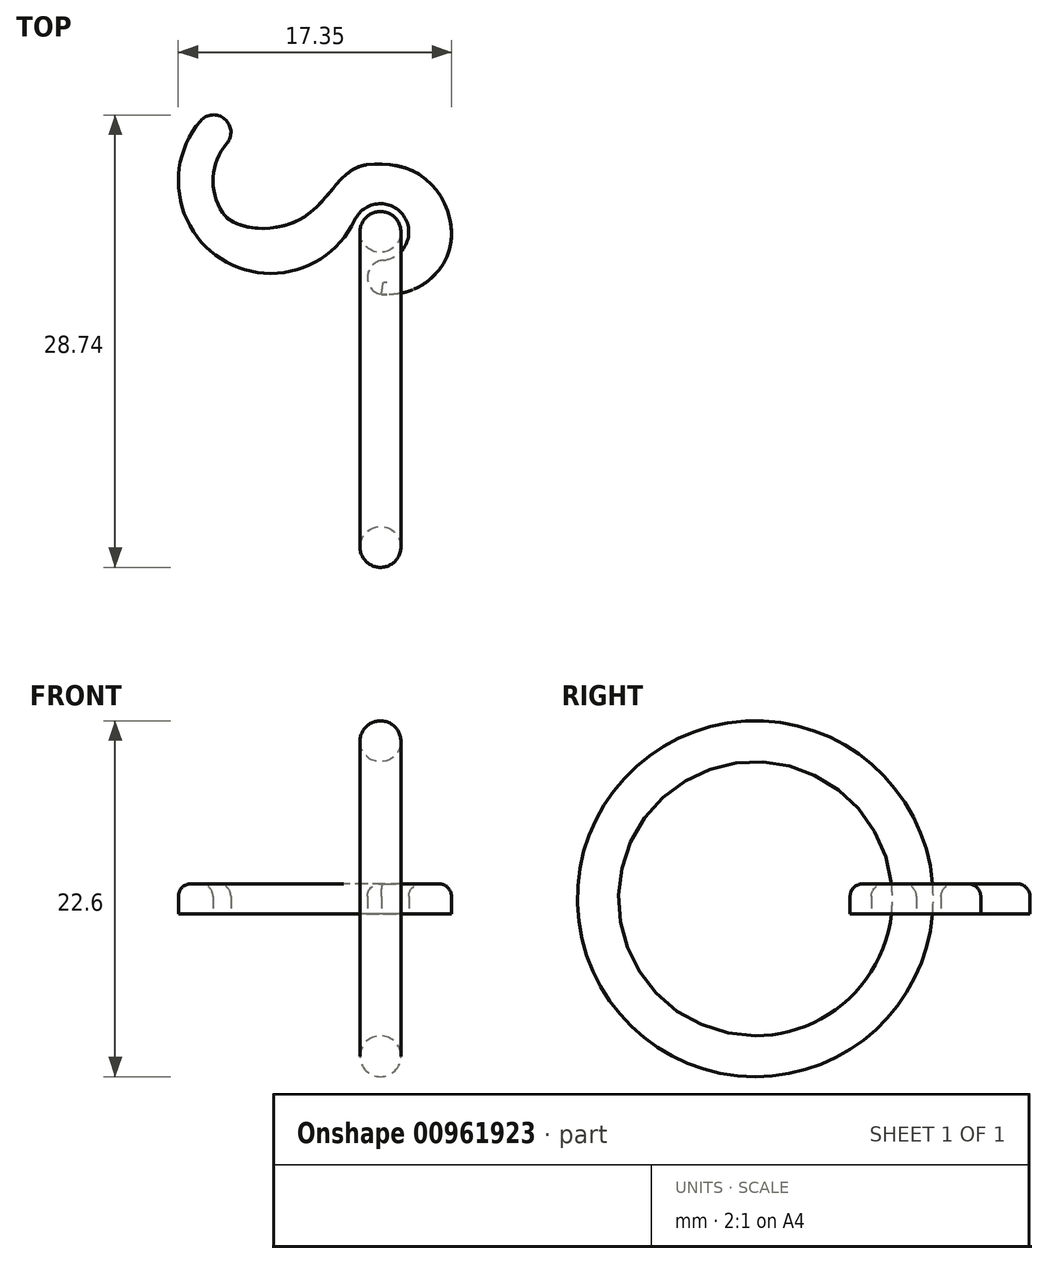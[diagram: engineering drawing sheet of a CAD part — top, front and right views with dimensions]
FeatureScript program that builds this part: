
annotation { "Feature Type Name" : "Feature", "Feature Type Description" : "" }
export const myFeature = defineFeature(function(context is Context, id is Id, definition is map)
    precondition{}
    {
        {
            var Q0;
            Q0=qCreatedBy(makeId("Top.planeOp"),FACE);
            var sketch = newSketch(context, id + "F0", { "sketchPlane" : qUnion([Q0])});
            skCircle(sketch, "E0", {"center": v(0, 10) * mm, "radius": 1.3 * mm});
            skLineSegment(sketch, "E1", {"start": v(0, 0) * mm, "end": v(-2.82, 0) * mm, "construction": true});
            skArc(sketch, "E2", {"start": v(0.27, 7.11) * mm, "mid": v(2.37, 11.67) * mm, "end": v(-2.63, 11.23) * mm});
            skArc(sketch, "E3.filletArc", {"start": v(-10.6, 16.34) * mm, "mid": v(-9.54, 9.23) * mm, "end": v(-2.63, 11.23) * mm});
            skLineSegment(sketch, "E4", {"start": v(0, 10) * mm, "end": v(-1.64, 5.37) * mm, "construction": true});
            skLineSegment(sketch, "E5", {"start": v(-0.83, 7.67) * mm, "end": v(-1.52, 5.72) * mm});
            skPoint(sketch, "E6.visualSharp", {"position": v(-0.97, 7.27) * mm});
            skArc(sketch, "E6.filletArc", {"start": v(0.27, 7.11) * mm, "mid": v(-0.83, 6.68) * mm, "end": v(-1.52, 5.72) * mm});
            skArc(sketch, "E7", {"start": v(-10.6, 16.34) * mm, "mid": v(-9.29, 17.42) * mm, "end": v(-7.69, 17.97) * mm});
            skArc(sketch, "E8", {"start": v(-7.69, 17.97) * mm, "mid": v(-5.06, 16.97) * mm, "end": v(-4.56, 14.21) * mm});
            skArc(sketch, "E9.0.startCap", {"start": v(-7.52, 16.88) * mm, "mid": v(-8.77, 17.8) * mm, "end": v(-7.85, 19.06) * mm});
            skArc(sketch, "E9.0.endCap", {"start": v(-3.52, 13.85) * mm, "mid": v(-4.92, 13.17) * mm, "end": v(-5.6, 14.57) * mm});
            skArc(sketch, "E9.0.left", {"start": v(-7.85, 19.06) * mm, "mid": v(-4.21, 17.68) * mm, "end": v(-3.52, 13.85) * mm});
            skArc(sketch, "E9.0.right", {"start": v(-7.52, 16.88) * mm, "mid": v(-5.9, 16.27) * mm, "end": v(-5.6, 14.57) * mm});
            skArc(sketch, "E9.1.startCap", {"start": v(-9.76, 15.63) * mm, "mid": v(-11.31, 15.5) * mm, "end": v(-11.44, 17.05) * mm});
            skArc(sketch, "E9.1.endCap", {"start": v(-7.85, 19.06) * mm, "mid": v(-6.6, 18.14) * mm, "end": v(-7.52, 16.88) * mm});
            skArc(sketch, "E9.1.left", {"start": v(-11.44, 17.05) * mm, "mid": v(-9.83, 18.38) * mm, "end": v(-7.85, 19.06) * mm});
            skArc(sketch, "E9.1.right", {"start": v(-9.76, 15.63) * mm, "mid": v(-8.75, 16.46) * mm, "end": v(-7.52, 16.88) * mm});
            skArc(sketch, "E9.2.startCap", {"start": v(-11.44, 17.05) * mm, "mid": v(-9.89, 17.18) * mm, "end": v(-9.76, 15.63) * mm});
            skArc(sketch, "E9.2.left", {"start": v(-9.76, 15.63) * mm, "mid": v(-10.63, 13.48) * mm, "end": v(-10.04, 11.24) * mm});
            skArc(sketch, "E9.2.right", {"start": v(-11.44, 17.05) * mm, "mid": v(-10.13, 8.3) * mm, "end": v(-1.63, 10.76) * mm});
            skArc(sketch, "E9.3.startCap", {"start": v(0.07, 6.03) * mm, "mid": v(-0.83, 7.16) * mm, "end": v(0.17, 8.2) * mm});
            skArc(sketch, "E9.3.left", {"start": v(0.17, 8.2) * mm, "mid": v(1.47, 11.04) * mm, "end": v(-1.63, 10.76) * mm});
            skFitSpline(sketch, "E10", {"points": [v(-10.04, 11.24) * mm, v(-5.03, 10.85) * mm, v(-0.87, 14.27) * mm], "startDerivative": vector(4.6, -7.08) * mm, "endDerivative": vector(9.85, 1.05) * mm});
            skArc(sketch, "E11.0.startCap", {"start": v(0.17, 8.2) * mm, "mid": v(1.36, 7.21) * mm, "end": v(0.37, 6.02) * mm});
            skArc(sketch, "E11.0.endCap", {"start": v(-0.48, 5.35) * mm, "mid": v(-1.89, 4.69) * mm, "end": v(-2.55, 6.09) * mm});
            skArc(sketch, "E11.0.left", {"start": v(0.37, 6.02) * mm, "mid": v(-0.15, 5.81) * mm, "end": v(-0.48, 5.35) * mm});
            skArc(sketch, "E11.0.right", {"start": v(0.17, 8.2) * mm, "mid": v(-1.5, 7.55) * mm, "end": v(-2.55, 6.09) * mm});
            skFitSpline(sketch, "E12", {"points": [v(-0.87, 14.27) * mm, v(2.63, 13.55) * mm, v(4.47, 9.32) * mm, v(0.07, 6.03) * mm], "startDerivative": vector(11.12, 1.18) * mm, "endDerivative": vector(-20.1, 1.27) * mm});
            skCircle(sketch, "E13", {"center": v(-3.16, 13.5) * mm, "radius": 0.5 * mm, "construction": true});
            skSolve(sketch);
        }
        {
            var Q0;
            Q0=makeQuery(id+"F0.imprint","IMPRINT",FACE,{"disambiguationData":[TD([[makeQuery(id+"F0.imprint","IMPRINT",EDGE,{"derivedFrom":sQuery(id+"F0.wireOp",EDGE,"E0")}),1.0]])]});
            var Q1;
            Q1=sQuery(id+"F0.wireOp",EDGE,"E1");
            revolve(context, id + "F1", {"surfaceOperationType" : NewSurfaceOperationType.NEW, "entities" : qUnion([Q0]), "axis" : qUnion([Q1]), "revolveType" : RevolveType.FULL});
        }
        {
            var Q0;
            {var subQ0=sQuery(id+"F0.wireOp",EDGE,"7e8b46de-5f97-4e43-a4e6-41a7d2c543f1.filletArc");var subQ1=sQuery(id+"F0.wireOp",EDGE,"XuSTN1GD-owKZ-Hfnf-Vevz-HP5xYmG9djur");var subQ2=makeQuery(id+"F0.imprint","INTERSECT",VERTEX,{"derivedFrom":[subQ1,subQ0]});Q0=makeQuery(id+"F0.imprint","IMPRINT",FACE,{"disambiguationData":[TD([[makeQuery(id+"F0.imprint","IMPRINT",EDGE,{"disambiguationData":[TD([[subQ2,-1.0]])],"derivedFrom":subQ1}),1.0]])]});}
            var Q1;
            {var subQ0=sQuery(id+"F0.wireOp",EDGE,"E6.filletArc");var subQ1=sQuery(id+"F0.wireOp",EDGE,"E2");var subQ2=makeQuery(id+"F0.imprint","INTERSECT",VERTEX,{"derivedFrom":[subQ1,subQ0]});Q1=makeQuery(id+"F0.imprint","IMPRINT",FACE,{"disambiguationData":[TD([[makeQuery(id+"F0.imprint","IMPRINT",EDGE,{"disambiguationData":[TD([[subQ2,-1.0]])],"derivedFrom":subQ1}),-1.0]])]});}
            var Q2;
            Q2=makeQuery(id+"F0.imprint","IMPRINT",FACE,{"disambiguationData":[TD([[makeQuery(id+"F0.imprint","IMPRINT",EDGE,{"derivedFrom":sQuery(id+"F0.wireOp",EDGE,"7d60ddda-c9f3-4b5c-aec7-61beb639432c.6.endCap")}),-1.0]])]});
            var Q3;
            {var subQ0=sQuery(id+"F0.wireOp",EDGE,"E3.filletArc");var subQ1=sQuery(id+"F0.wireOp",EDGE,"E2");var subQ2=makeQuery(id+"F0.imprint","INTERSECT",VERTEX,{"derivedFrom":[subQ1,subQ0]});Q3=makeQuery(id+"F0.imprint","IMPRINT",FACE,{"disambiguationData":[TD([[makeQuery(id+"F0.imprint","IMPRINT",EDGE,{"disambiguationData":[TD([[subQ2,1.0]])],"derivedFrom":subQ1}),-1.0]])]});}
            var Q4;
            {var subQ0=sQuery(id+"F0.wireOp",EDGE,"E6.filletArc");var subQ1=sQuery(id+"F0.wireOp",EDGE,"E2");var subQ2=makeQuery(id+"F0.imprint","INTERSECT",VERTEX,{"derivedFrom":[subQ1,subQ0]});Q4=makeQuery(id+"F0.imprint","IMPRINT",FACE,{"disambiguationData":[TD([[makeQuery(id+"F0.imprint","IMPRINT",EDGE,{"disambiguationData":[TD([[subQ2,-1.0]])],"derivedFrom":subQ1}),1.0]])]});}
            var Q5;
            {var subQ0=sQuery(id+"F0.wireOp",EDGE,"2rV7FZ9r-o5Y1-5ZDM-YBhN-Ku4Qg7FZG19c");var subQ1=sQuery(id+"F0.wireOp",EDGE,"XuSTN1GD-owKZ-Hfnf-Vevz-HP5xYmG9djur");var subQ2=makeQuery(id+"F0.imprint","INTERSECT",VERTEX,{"derivedFrom":[subQ1,subQ0]});Q5=makeQuery(id+"F0.imprint","IMPRINT",FACE,{"disambiguationData":[TD([[makeQuery(id+"F0.imprint","IMPRINT",EDGE,{"disambiguationData":[TD([[subQ2,1.0]])],"derivedFrom":subQ1}),1.0]])]});}
            var Q6;
            {var subQ5=sQuery(id+"F0.wireOp",EDGE,"7d60ddda-c9f3-4b5c-aec7-61beb639432c.2.right");Q6=makeQuery(id+"F0.imprint","IMPRINT",FACE,{"disambiguationData":[TD([[makeQuery(id+"F0.imprint","IMPRINT",EDGE,{"derivedFrom":subQ5}),1.0]])]});}
            var Q7;
            {var subQ5=sQuery(id+"F0.wireOp",EDGE,"gjqhSW9i-IF4X-P20h-zRvC-4p3DaIg5BdPQ");Q7=makeQuery(id+"F0.imprint","IMPRINT",FACE,{"disambiguationData":[TD([[makeQuery(id+"F0.imprint","IMPRINT",EDGE,{"derivedFrom":subQ5}),-1.0]])]});}
            var Q8;
            {var subQ0=sQuery(id+"F0.wireOp",EDGE,"7d60ddda-c9f3-4b5c-aec7-61beb639432c.2.endCap");var subQ1=sQuery(id+"F0.wireOp",EDGE,"E3.filletArc");var subQ2=makeQuery(id+"F0.imprint","INTERSECT",VERTEX,{"derivedFrom":[subQ1,subQ0]});Q8=makeQuery(id+"F0.imprint","IMPRINT",FACE,{"disambiguationData":[TD([[makeQuery(id+"F0.imprint","IMPRINT",EDGE,{"disambiguationData":[TD([[subQ2,-1.0]])],"derivedFrom":subQ1}),-1.0]])]});}
            var Q9;
            {var subQ0=sQuery(id+"F0.wireOp",EDGE,"E3.filletArc");var subQ1=sQuery(id+"F0.wireOp",EDGE,"E2");var subQ2=makeQuery(id+"F0.imprint","INTERSECT",VERTEX,{"derivedFrom":[subQ1,subQ0]});Q9=makeQuery(id+"F0.imprint","IMPRINT",FACE,{"disambiguationData":[TD([[makeQuery(id+"F0.imprint","IMPRINT",EDGE,{"disambiguationData":[TD([[subQ2,1.0]])],"derivedFrom":subQ1}),1.0]])]});}
            var Q10;
            {var subQ5=sQuery(id+"F0.wireOp",EDGE,"7d60ddda-c9f3-4b5c-aec7-61beb639432c.4.left");Q10=makeQuery(id+"F0.imprint","IMPRINT",FACE,{"disambiguationData":[TD([[makeQuery(id+"F0.imprint","IMPRINT",EDGE,{"derivedFrom":subQ5}),-1.0]])]});}
            var Q11;
            {var subQ7=sQuery(id+"F0.wireOp",EDGE,"gjqhSW9i-IF4X-P20h-zRvC-4p3DaIg5BdPQ");Q11=makeQuery(id+"F0.imprint","IMPRINT",FACE,{"disambiguationData":[TD([[makeQuery(id+"F0.imprint","IMPRINT",EDGE,{"derivedFrom":subQ7}),1.0]])]});}
            var Q12;
            {var subQ0=sQuery(id+"F0.wireOp",EDGE,"2rV7FZ9r-o5Y1-5ZDM-YBhN-Ku4Qg7FZG19c");var subQ1=sQuery(id+"F0.wireOp",EDGE,"XuSTN1GD-owKZ-Hfnf-Vevz-HP5xYmG9djur");var subQ2=makeQuery(id+"F0.imprint","INTERSECT",VERTEX,{"derivedFrom":[subQ1,subQ0]});Q12=makeQuery(id+"F0.imprint","IMPRINT",FACE,{"disambiguationData":[TD([[makeQuery(id+"F0.imprint","IMPRINT",EDGE,{"disambiguationData":[TD([[subQ2,1.0]])],"derivedFrom":subQ1}),-1.0]])]});}
            var Q13;
            {var subQ5=sQuery(id+"F0.wireOp",EDGE,"7d60ddda-c9f3-4b5c-aec7-61beb639432c.1.right");Q13=makeQuery(id+"F0.imprint","IMPRINT",FACE,{"disambiguationData":[TD([[makeQuery(id+"F0.imprint","IMPRINT",EDGE,{"derivedFrom":subQ5}),1.0]])]});}
            var Q14;
            Q14=makeQuery(id+"F0.imprint","IMPRINT",FACE,{"disambiguationData":[TD([[makeQuery(id+"F0.imprint","IMPRINT",EDGE,{"derivedFrom":sQuery(id+"F0.wireOp",EDGE,"7d60ddda-c9f3-4b5c-aec7-61beb639432c.0.endCap")}),-1.0]])]});
            var Q15;
            {var subQ5=sQuery(id+"F0.wireOp",EDGE,"7d60ddda-c9f3-4b5c-aec7-61beb639432c.1.left");Q15=makeQuery(id+"F0.imprint","IMPRINT",FACE,{"disambiguationData":[TD([[makeQuery(id+"F0.imprint","IMPRINT",EDGE,{"derivedFrom":subQ5}),-1.0]])]});}
            var Q16;
            {var subQ5=sQuery(id+"F0.wireOp",EDGE,"7d60ddda-c9f3-4b5c-aec7-61beb639432c.5.left");Q16=makeQuery(id+"F0.imprint","IMPRINT",FACE,{"disambiguationData":[TD([[makeQuery(id+"F0.imprint","IMPRINT",EDGE,{"derivedFrom":subQ5}),-1.0]])]});}
            var Q17;
            {var subQ5=sQuery(id+"F0.wireOp",EDGE,"7d60ddda-c9f3-4b5c-aec7-61beb639432c.4.right");Q17=makeQuery(id+"F0.imprint","IMPRINT",FACE,{"disambiguationData":[TD([[makeQuery(id+"F0.imprint","IMPRINT",EDGE,{"derivedFrom":subQ5}),1.0]])]});}
            var Q18;
            {var subQ0=sQuery(id+"F0.wireOp",EDGE,"7e8b46de-5f97-4e43-a4e6-41a7d2c543f1.filletArc");var subQ1=sQuery(id+"F0.wireOp",EDGE,"XuSTN1GD-owKZ-Hfnf-Vevz-HP5xYmG9djur");var subQ2=makeQuery(id+"F0.imprint","INTERSECT",VERTEX,{"derivedFrom":[subQ1,subQ0]});Q18=makeQuery(id+"F0.imprint","IMPRINT",FACE,{"disambiguationData":[TD([[makeQuery(id+"F0.imprint","IMPRINT",EDGE,{"disambiguationData":[TD([[subQ2,-1.0]])],"derivedFrom":subQ1}),-1.0]])]});}
            var Q19;
            {var subQ5=sQuery(id+"F0.wireOp",EDGE,"7d60ddda-c9f3-4b5c-aec7-61beb639432c.5.right");Q19=makeQuery(id+"F0.imprint","IMPRINT",FACE,{"disambiguationData":[TD([[makeQuery(id+"F0.imprint","IMPRINT",EDGE,{"derivedFrom":subQ5}),1.0]])]});}
            var Q20;
            {var subQ5=sQuery(id+"F0.wireOp",EDGE,"7d60ddda-c9f3-4b5c-aec7-61beb639432c.2.left");Q20=makeQuery(id+"F0.imprint","IMPRINT",FACE,{"disambiguationData":[TD([[makeQuery(id+"F0.imprint","IMPRINT",EDGE,{"derivedFrom":subQ5}),-1.0]])]});}
            var Q21;
            {var subQ0=sQuery(id+"F0.wireOp",EDGE,"7d60ddda-c9f3-4b5c-aec7-61beb639432c.3.endCap");var subQ1=sQuery(id+"F0.wireOp",EDGE,"7e8b46de-5f97-4e43-a4e6-41a7d2c543f1.filletArc");var subQ2=makeQuery(id+"F0.imprint","INTERSECT",VERTEX,{"derivedFrom":[subQ1,subQ0]});Q21=makeQuery(id+"F0.imprint","IMPRINT",FACE,{"disambiguationData":[TD([[makeQuery(id+"F0.imprint","IMPRINT",EDGE,{"disambiguationData":[TD([[subQ2,-1.0]])],"derivedFrom":subQ1}),1.0]])]});}
            var Q22;
            {var subQ0=sQuery(id+"F0.wireOp",EDGE,"7d60ddda-c9f3-4b5c-aec7-61beb639432c.3.endCap");var subQ1=sQuery(id+"F0.wireOp",EDGE,"7e8b46de-5f97-4e43-a4e6-41a7d2c543f1.filletArc");var subQ2=makeQuery(id+"F0.imprint","INTERSECT",VERTEX,{"derivedFrom":[subQ1,subQ0]});Q22=makeQuery(id+"F0.imprint","IMPRINT",FACE,{"disambiguationData":[TD([[makeQuery(id+"F0.imprint","IMPRINT",EDGE,{"disambiguationData":[TD([[subQ2,-1.0]])],"derivedFrom":subQ1}),-1.0]])]});}
            var Q23;
            {var subQ0=sQuery(id+"F0.wireOp",EDGE,"7d60ddda-c9f3-4b5c-aec7-61beb639432c.2.endCap");var subQ1=sQuery(id+"F0.wireOp",EDGE,"E3.filletArc");var subQ2=makeQuery(id+"F0.imprint","INTERSECT",VERTEX,{"derivedFrom":[subQ1,subQ0]});Q23=makeQuery(id+"F0.imprint","IMPRINT",FACE,{"disambiguationData":[TD([[makeQuery(id+"F0.imprint","IMPRINT",EDGE,{"disambiguationData":[TD([[subQ2,-1.0]])],"derivedFrom":subQ1}),1.0]])]});}
            var Q24;
            {var subQ0=sQuery(id+"F0.wireOp",EDGE,"7d60ddda-c9f3-4b5c-aec7-61beb639432c.3.left");Q24=makeQuery(id+"F0.imprint","IMPRINT",FACE,{"disambiguationData":[TD([[makeQuery(id+"F0.imprint","IMPRINT",EDGE,{"derivedFrom":subQ0}),-1.0]])]});}
            var Q25;
            {var subQ0=sQuery(id+"F0.wireOp",EDGE,"7d60ddda-c9f3-4b5c-aec7-61beb639432c.3.right");Q25=makeQuery(id+"F0.imprint","IMPRINT",FACE,{"disambiguationData":[TD([[makeQuery(id+"F0.imprint","IMPRINT",EDGE,{"derivedFrom":subQ0}),1.0]])]});}
            var Q26;
            {var subQ0=sQuery(id+"F0.wireOp",EDGE,"3c797257-ffbf-45d1-a8b6-85a41e315347.0.startCap");var subQ1=sQuery(id+"F0.wireOp",EDGE,"E3.filletArc");var subQ2=makeQuery(id+"F0.imprint","INTERSECT",VERTEX,{"derivedFrom":[subQ1,subQ0]});Q26=makeQuery(id+"F0.imprint","IMPRINT",FACE,{"disambiguationData":[TD([[makeQuery(id+"F0.imprint","IMPRINT",EDGE,{"disambiguationData":[TD([[subQ2,-1.0]])],"derivedFrom":subQ1}),-1.0]])]});}
            var Q27;
            {var subQ0=sQuery(id+"F0.wireOp",EDGE,"0f0b0a7c-fbad-4233-8603-baac45b0bff0");var subQ1=sQuery(id+"F0.wireOp",EDGE,"E3.filletArc");var subQ2=makeQuery(id+"F0.imprint","INTERSECT",VERTEX,{"derivedFrom":[subQ1,subQ0]});Q27=makeQuery(id+"F0.imprint","IMPRINT",FACE,{"disambiguationData":[TD([[makeQuery(id+"F0.imprint","IMPRINT",EDGE,{"disambiguationData":[TD([[subQ2,-1.0]])],"derivedFrom":subQ1}),1.0]])]});}
            var Q28;
            {var subQ1=sQuery(id+"F0.wireOp",EDGE,"7d60ddda-c9f3-4b5c-aec7-61beb639432c.4.left");var subQ3=sQuery(id+"F0.wireOp",EDGE,"3c797257-ffbf-45d1-a8b6-85a41e315347.0.right");var subQ4=makeQuery(id+"F0.imprint","INTERSECT",VERTEX,{"derivedFrom":[subQ1,subQ3]});Q28=makeQuery(id+"F0.imprint","IMPRINT",FACE,{"disambiguationData":[TD([[makeQuery(id+"F0.imprint","IMPRINT",EDGE,{"disambiguationData":[TD([[subQ4,-1.0]])],"derivedFrom":subQ1}),-1.0]])]});}
            var Q29;
            {var subQ1=sQuery(id+"F0.wireOp",EDGE,"7d60ddda-c9f3-4b5c-aec7-61beb639432c.3.startCap");var subQ3=sQuery(id+"F0.wireOp",EDGE,"7d60ddda-c9f3-4b5c-aec7-61beb639432c.3.endCap");var subQ4=makeQuery(id+"F0.imprint","INTERSECT",VERTEX,{"disambiguationData":[OD(0.0)],"derivedFrom":[subQ1,subQ3]});Q29=makeQuery(id+"F0.imprint","IMPRINT",FACE,{"disambiguationData":[TD([[makeQuery(id+"F0.imprint","IMPRINT",EDGE,{"disambiguationData":[TD([[subQ4,1.0]])],"derivedFrom":subQ3}),1.0]])]});}
            var Q30;
            {var subQ6=sQuery(id+"F0.wireOp",EDGE,"7d60ddda-c9f3-4b5c-aec7-61beb639432c.3.startCap");var subQ8=sQuery(id+"F0.wireOp",EDGE,"E3.filletArc");var subQ9=makeQuery(id+"F0.imprint","INTERSECT",VERTEX,{"derivedFrom":[subQ8,subQ6]});Q30=makeQuery(id+"F0.imprint","IMPRINT",FACE,{"disambiguationData":[TD([[makeQuery(id+"F0.imprint","IMPRINT",EDGE,{"disambiguationData":[TD([[subQ9,-1.0]])],"derivedFrom":subQ8}),1.0]])]});}
            var Q31;
            {var subQ0=sQuery(id+"F0.wireOp",EDGE,"7d60ddda-c9f3-4b5c-aec7-61beb639432c.3.startCap");var subQ1=sQuery(id+"F0.wireOp",EDGE,"E3.filletArc");var subQ2=makeQuery(id+"F0.imprint","INTERSECT",VERTEX,{"derivedFrom":[subQ1,subQ0]});Q31=makeQuery(id+"F0.imprint","IMPRINT",FACE,{"disambiguationData":[TD([[makeQuery(id+"F0.imprint","IMPRINT",EDGE,{"disambiguationData":[TD([[subQ2,-1.0]])],"derivedFrom":subQ1}),-1.0]])]});}
            var Q32;
            {var subQ0=sQuery(id+"F0.wireOp",EDGE,"7d60ddda-c9f3-4b5c-aec7-61beb639432c.3.endCap");var subQ1=sQuery(id+"F0.wireOp",EDGE,"7d60ddda-c9f3-4b5c-aec7-61beb639432c.3.startCap");var subQ2=makeQuery(id+"F0.imprint","INTERSECT",VERTEX,{"disambiguationData":[OD(1.0)],"derivedFrom":[subQ1,subQ0]});Q32=makeQuery(id+"F0.imprint","IMPRINT",FACE,{"disambiguationData":[TD([[makeQuery(id+"F0.imprint","IMPRINT",EDGE,{"disambiguationData":[TD([[subQ2,-1.0]])],"derivedFrom":subQ1}),-1.0]])]});}
            var Q33;
            {var subQ5=sQuery(id+"F0.wireOp",EDGE,"3c797257-ffbf-45d1-a8b6-85a41e315347.0.endCap");Q33=makeQuery(id+"F0.imprint","IMPRINT",FACE,{"disambiguationData":[TD([[makeQuery(id+"F0.imprint","IMPRINT",EDGE,{"derivedFrom":subQ5}),-1.0]])]});}
            var Q34;
            {var subQ5=sQuery(id+"F0.wireOp",EDGE,"E9.1.right");Q34=makeQuery(id+"F0.imprint","IMPRINT",FACE,{"disambiguationData":[TD([[makeQuery(id+"F0.imprint","IMPRINT",EDGE,{"derivedFrom":subQ5}),1.0]])]});}
            var Q35;
            {var subQ5=sQuery(id+"F0.wireOp",EDGE,"E9.1.left");Q35=makeQuery(id+"F0.imprint","IMPRINT",FACE,{"disambiguationData":[TD([[makeQuery(id+"F0.imprint","IMPRINT",EDGE,{"derivedFrom":subQ5}),-1.0]])]});}
            var Q36;
            Q36=makeQuery(id+"F0.imprint","IMPRINT",FACE,{"disambiguationData":[TD([[makeQuery(id+"F0.imprint","IMPRINT",EDGE,{"derivedFrom":sQuery(id+"F0.wireOp",EDGE,"E9.0.endCap")}),-1.0]])]});
            var Q37;
            {var subQ0=sQuery(id+"F0.wireOp",EDGE,"E8");var subQ1=sQuery(id+"F0.wireOp",EDGE,"E7");var subQ2=makeQuery(id+"F0.imprint","INTERSECT",VERTEX,{"derivedFrom":[subQ1,subQ0]});Q37=makeQuery(id+"F0.imprint","IMPRINT",FACE,{"disambiguationData":[TD([[makeQuery(id+"F0.imprint","IMPRINT",EDGE,{"disambiguationData":[TD([[subQ2,1.0]])],"derivedFrom":subQ1}),1.0]])]});}
            var Q38;
            {var subQ0=sQuery(id+"F0.wireOp",EDGE,"E8");var subQ1=sQuery(id+"F0.wireOp",EDGE,"E7");var subQ2=makeQuery(id+"F0.imprint","INTERSECT",VERTEX,{"derivedFrom":[subQ1,subQ0]});Q38=makeQuery(id+"F0.imprint","IMPRINT",FACE,{"disambiguationData":[TD([[makeQuery(id+"F0.imprint","IMPRINT",EDGE,{"disambiguationData":[TD([[subQ2,1.0]])],"derivedFrom":subQ1}),-1.0]])]});}
            var Q39;
            {var subQ5=sQuery(id+"F0.wireOp",EDGE,"E9.3.right");Q39=makeQuery(id+"F0.imprint","IMPRINT",FACE,{"disambiguationData":[TD([[makeQuery(id+"F0.imprint","IMPRINT",EDGE,{"derivedFrom":subQ5}),1.0]])]});}
            var Q40;
            {var subQ5=sQuery(id+"F0.wireOp",EDGE,"E9.3.left");Q40=makeQuery(id+"F0.imprint","IMPRINT",FACE,{"disambiguationData":[TD([[makeQuery(id+"F0.imprint","IMPRINT",EDGE,{"derivedFrom":subQ5}),-1.0]])]});}
            var Q41;
            Q41=makeQuery(id+"F0.imprint","IMPRINT",FACE,{"disambiguationData":[TD([[makeQuery(id+"F0.imprint","IMPRINT",EDGE,{"derivedFrom":sQuery(id+"F0.wireOp",EDGE,"43b14571-7811-4a92-9948-5e085ce3c61c.0.endCap")}),-1.0]])]});
            var Q42;
            Q42=makeQuery(id+"F0.imprint","IMPRINT",FACE,{"disambiguationData":[TD([[makeQuery(id+"F0.imprint","IMPRINT",EDGE,{"derivedFrom":sQuery(id+"F0.wireOp",EDGE,"E11.0.endCap")}),-1.0]])]});
            extrude(context, id + "F2", {"entities" : qUnion([Q0, Q1, Q2, Q3, Q4, Q5, Q6, Q7, Q8, Q9, Q10, Q11, Q12, Q13, Q14, Q15, Q16, Q17, Q18, Q19, Q20, Q21, Q22, Q23, Q24, Q25, Q26, Q27, Q28, Q29, Q30, Q31, Q32, Q33, Q34, Q35, Q36, Q37, Q38, Q39, Q40, Q41, Q42]), "endBound" : BoundingType.SYMMETRIC, "depth" : 1.9 * mm, "offsetDistance" : 25 * mm});
        }
        {
            var Q0;
            Q0=makeQuery(id+"F2.opExtrude","CAP_EDGE",EDGE,{"disambiguationData":[OSD([sQuery(id+"F0.wireOp",EDGE,"E10")])],"isStart":false});
            var Q1;
            Q1=makeQuery(id+"F2.opExtrude","CAP_EDGE",EDGE,{"disambiguationData":[OSD([sQuery(id+"F0.wireOp",EDGE,"E9.0.right")])],"isStart":true});
            fillet(context, id + "F3", {"entities" : qUnion([Q0, Q1]), "radius" : 0.8 * mm, "tangentPropagation" : true, "allowEdgeOverflow" : false});
        }
    });
